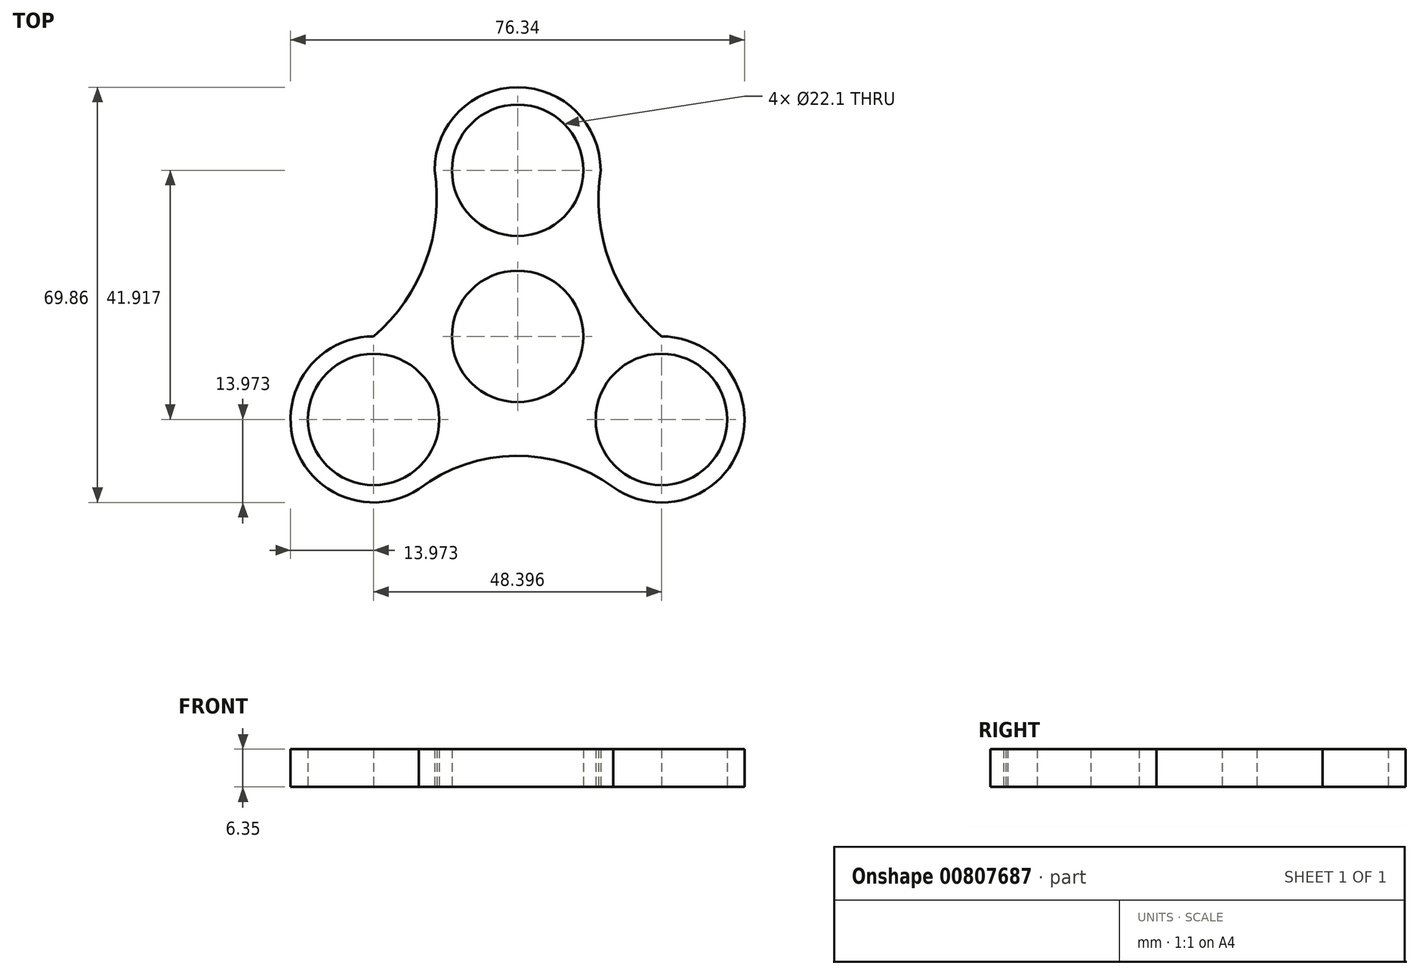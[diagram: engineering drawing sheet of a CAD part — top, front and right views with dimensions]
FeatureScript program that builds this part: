
annotation { "Feature Type Name" : "Feature", "Feature Type Description" : "" }
export const myFeature = defineFeature(function(context is Context, id is Id, definition is map)
    precondition{}
    {
        {
            var Q0;
            Q0=qCreatedBy(makeId("Top.planeOp"),FACE);
            var sketch = newSketch(context, id + "F0", { "sketchPlane" : qUnion([Q0])});
            skCircle(sketch, "E0", {"center": v(0, 0) * mm, "radius": 11.05 * mm});
            skLineSegment(sketch, "E1", {"start": v(0, 0) * mm, "end": v(0, 27.94) * mm, "construction": true});
            skCircle(sketch, "E2", {"center": v(0, 27.94) * mm, "radius": 11.05 * mm});
            skCircle(sketch, "E3.1.0", {"center": v(-24.2, -13.97) * mm, "radius": 11.05 * mm});
            skCircle(sketch, "E3.2.0", {"center": v(24.19, -13.98) * mm, "radius": 11.05 * mm});
            skCircle(sketch, "E4", {"center": v(0, 27.94) * mm, "radius": 13.97 * mm});
            skCircle(sketch, "E5", {"center": v(24.19, -13.98) * mm, "radius": 13.97 * mm});
            skCircle(sketch, "E6", {"center": v(-24.2, -13.97) * mm, "radius": 13.97 * mm});
            skLineSegment(sketch, "E7", {"start": v(-24.2, -13.97) * mm, "end": v(-24.2, 0) * mm, "construction": true});
            skLineSegment(sketch, "E8", {"start": v(24.19, -13.98) * mm, "end": v(24.19, 0) * mm, "construction": true});
            skLineSegment(sketch, "E9", {"start": v(0, 27.94) * mm, "end": v(-13.97, 27.94) * mm, "construction": true});
            skLineSegment(sketch, "E10", {"start": v(0, 27.94) * mm, "end": v(13.97, 27.94) * mm, "construction": true});
            skLineSegment(sketch, "E11", {"start": v(24.19, -13.98) * mm, "end": v(24.19, -27.95) * mm, "construction": true});
            skLineSegment(sketch, "E12", {"start": v(-24.2, -13.97) * mm, "end": v(-24.2, -27.94) * mm, "construction": true});
            skLineSegment(sketch, "E13", {"start": v(24.19, -13.98) * mm, "end": v(10.22, -13.98) * mm, "construction": true});
            skLineSegment(sketch, "E14", {"start": v(-24.2, -13.97) * mm, "end": v(-10.24, -13.97) * mm, "construction": true});
            skLineSegment(sketch, "E15", {"start": v(-10.24, -13.97) * mm, "end": v(-16.63, -25.7) * mm, "construction": true});
            skLineSegment(sketch, "E16", {"start": v(10.22, -13.98) * mm, "end": v(16.08, -25.35) * mm, "construction": true});
            skArc(sketch, "E17", {"start": v(16.08, -25.35) * mm, "mid": v(-0.33, -20.09) * mm, "end": v(-16.63, -25.7) * mm});
            skArc(sketch, "E18", {"start": v(-24.2, 0) * mm, "mid": v(-15.45, 12.64) * mm, "end": v(-13.97, 27.94) * mm});
            skArc(sketch, "E19", {"start": v(13.97, 27.94) * mm, "mid": v(15.44, 12.63) * mm, "end": v(24.19, 0) * mm});
            skSolve(sketch);
        }
        {
            var Q0;
            Q0=makeQuery(id+"F0.imprint","IMPRINT",FACE,{"disambiguationData":[TD([[makeQuery(id+"F0.imprint","IMPRINT",EDGE,{"derivedFrom":sQuery(id+"F0.wireOp",EDGE,"E0")}),-1.0]])]});
            var Q1;
            Q1=makeQuery(id+"F0.imprint","IMPRINT",FACE,{"disambiguationData":[TD([[makeQuery(id+"F0.imprint","IMPRINT",EDGE,{"derivedFrom":sQuery(id+"F0.wireOp",EDGE,"E3.1.0")}),-1.0]])]});
            var Q2;
            Q2=makeQuery(id+"F0.imprint","IMPRINT",FACE,{"disambiguationData":[TD([[makeQuery(id+"F0.imprint","IMPRINT",EDGE,{"derivedFrom":sQuery(id+"F0.wireOp",EDGE,"E3.2.0")}),-1.0]])]});
            var Q3;
            Q3=makeQuery(id+"F0.imprint","IMPRINT",FACE,{"disambiguationData":[TD([[makeQuery(id+"F0.imprint","IMPRINT",EDGE,{"derivedFrom":sQuery(id+"F0.wireOp",EDGE,"E2")}),-1.0]])]});
            extrude(context, id + "F1", {"entities" : qUnion([Q0, Q1, Q2, Q3]), "depth" : 6.35 * mm, "offsetDistance" : 25.4 * mm});
        }
    });
